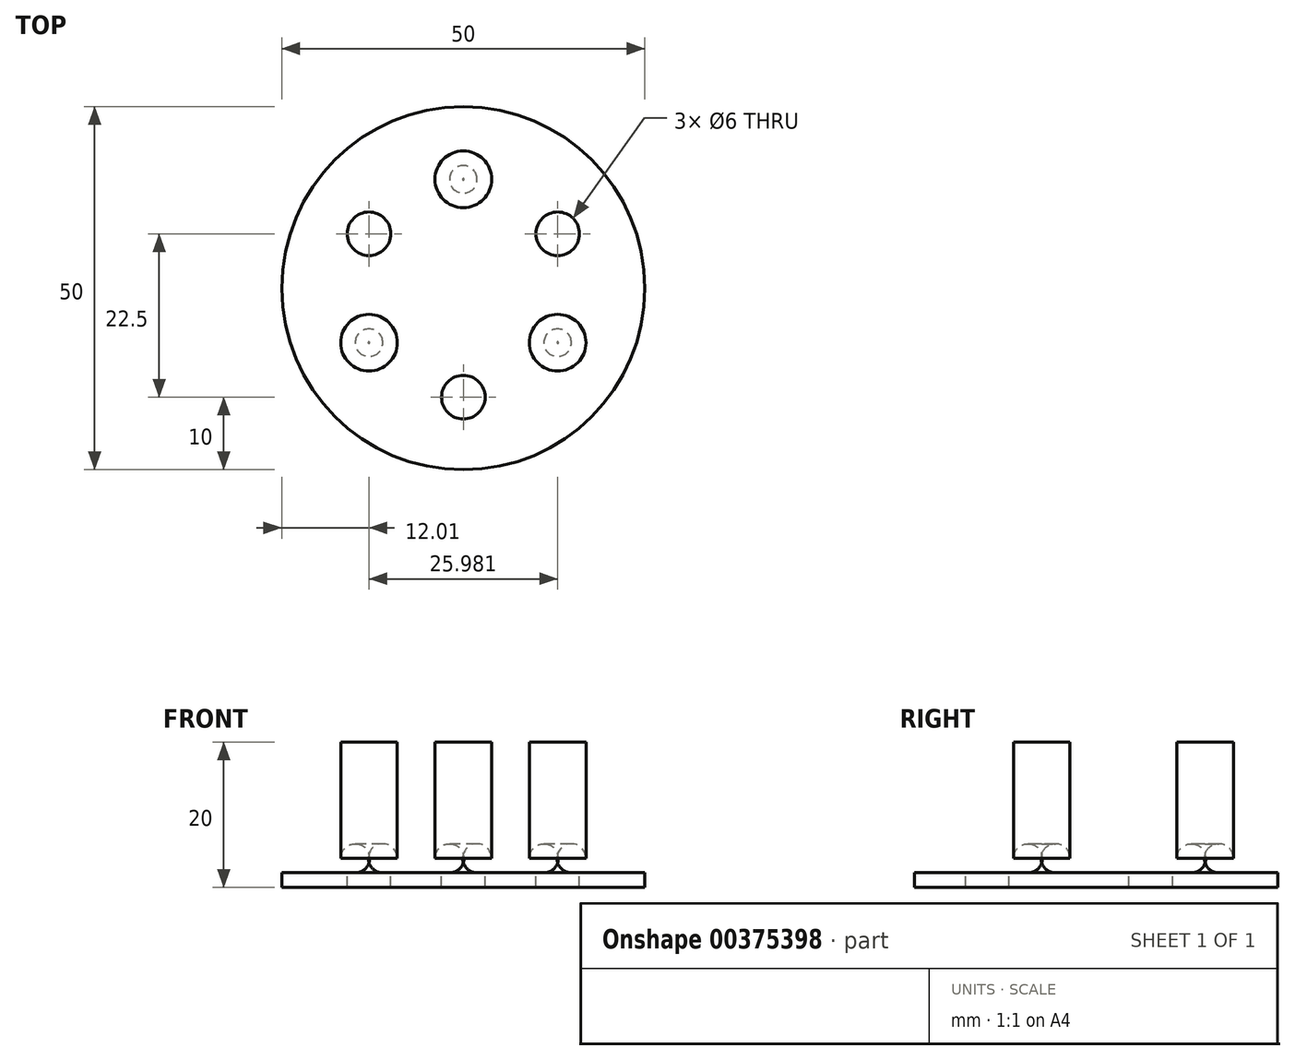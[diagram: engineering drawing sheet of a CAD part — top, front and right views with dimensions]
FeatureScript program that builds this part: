
annotation { "Feature Type Name" : "Feature", "Feature Type Description" : "" }
export const myFeature = defineFeature(function(context is Context, id is Id, definition is map)
    precondition{}
    {
        {
            var Q0;
            Q0=qCreatedBy(makeId("Top.planeOp"),FACE);
            var sketch = newSketch(context, id + "F0", { "sketchPlane" : qUnion([Q0])});
            skCircle(sketch, "E0", {"center": v(0, 0) * mm, "radius": 25 * mm});
            skCircle(sketch, "E1", {"center": v(0, 15) * mm, "radius": 3.9 * mm});
            skCircle(sketch, "E2", {"center": v(0, 0) * mm, "radius": 3.5 * mm});
            skCircle(sketch, "E3.1.0", {"center": v(-13, -7.5) * mm, "radius": 3.9 * mm});
            skCircle(sketch, "E3.2.0", {"center": v(13, -7.5) * mm, "radius": 3.9 * mm});
            skLineSegment(sketch, "E4", {"start": v(0, 15) * mm, "end": v(13, -7.5) * mm, "construction": true});
            skLineSegment(sketch, "E5", {"start": v(0, 0) * mm, "end": v(13, 7.5) * mm, "construction": true});
            skCircle(sketch, "E6", {"center": v(13, 7.5) * mm, "radius": 3 * mm});
            skCircle(sketch, "E7.1.0", {"center": v(-13, 7.5) * mm, "radius": 3 * mm});
            skCircle(sketch, "E7.2.0", {"center": v(0, -15) * mm, "radius": 3 * mm});
            skSolve(sketch);
        }
        {
            var Q0;
            Q0=qCreatedBy(makeId("Top.planeOp"),FACE);
            var sketch = newSketch(context, id + "F1", { "sketchPlane" : qUnion([Q0])});
            skCircle(sketch, "E8", {"center": v(0, 0) * mm, "radius": 25 * mm});
            skSolve(sketch);
        }
        {
            var Q0;
            Q0 = qSketchRegion(id + "F1", true);
            extrude(context, id + "F2", {"entities" : qUnion([Q0]), "oppositeDirection" : true, "depth" : 2 * mm});
        }
        {
            var Q0;
            Q0=makeQuery(id+"F0.imprint","IMPRINT",FACE,{"disambiguationData":[TD([[makeQuery(id+"F0.imprint","IMPRINT",EDGE,{"derivedFrom":sQuery(id+"F0.wireOp",EDGE,"E3.1.0")}),1.0]])]});
            var Q1;
            Q1=makeQuery(id+"F0.imprint","IMPRINT",FACE,{"disambiguationData":[TD([[makeQuery(id+"F0.imprint","IMPRINT",EDGE,{"derivedFrom":sQuery(id+"F0.wireOp",EDGE,"E1")}),1.0]])]});
            var Q2;
            Q2=makeQuery(id+"F0.imprint","IMPRINT",FACE,{"disambiguationData":[TD([[makeQuery(id+"F0.imprint","IMPRINT",EDGE,{"derivedFrom":sQuery(id+"F0.wireOp",EDGE,"E3.2.0")}),1.0]])]});
            extrude(context, id + "F3", {"entities" : qUnion([Q0, Q1, Q2]), "depth" : 18 * mm});
        }
        {
            var Q0;
            Q0=makeQuery(id+"F3.opExtrude","CAP_EDGE",EDGE,{"disambiguationData":[OSD([sQuery(id+"F0.wireOp",EDGE,"E3.2.0")])],"isStart":true});
            var Q1;
            Q1=makeQuery(id+"F3.opExtrude","CAP_EDGE",EDGE,{"disambiguationData":[OSD([sQuery(id+"F0.wireOp",EDGE,"E1")])],"isStart":true});
            var Q2;
            Q2=makeQuery(id+"F3.opExtrude","CAP_EDGE",EDGE,{"disambiguationData":[OSD([sQuery(id+"F0.wireOp",EDGE,"E3.1.0")])],"isStart":true});
            fillet(context, id + "F4", {"entities" : qUnion([Q0, Q1, Q2]), "radius" : 2 * mm, "tangentPropagation" : true, "allowEdgeOverflow" : false});
        }
        {
            var Q0;
            Q0=makeQuery(id+"F0.imprint","IMPRINT",FACE,{"disambiguationData":[TD([[makeQuery(id+"F0.imprint","IMPRINT",EDGE,{"derivedFrom":sQuery(id+"F0.wireOp",EDGE,"E6")}),1.0]])]});
            var Q1;
            Q1=makeQuery(id+"F0.imprint","IMPRINT",FACE,{"disambiguationData":[TD([[makeQuery(id+"F0.imprint","IMPRINT",EDGE,{"derivedFrom":sQuery(id+"F0.wireOp",EDGE,"E7.1.0")}),1.0]])]});
            var Q2;
            Q2=makeQuery(id+"F0.imprint","IMPRINT",FACE,{"disambiguationData":[TD([[makeQuery(id+"F0.imprint","IMPRINT",EDGE,{"derivedFrom":sQuery(id+"F0.wireOp",EDGE,"E7.2.0")}),1.0]])]});
            extrude(context, id + "F5", {"entities" : qUnion([Q0, Q1, Q2]), "operationType" : NewBodyOperationType.REMOVE, "oppositeDirection" : true, "depth" : 2 * mm});
        }
    });
